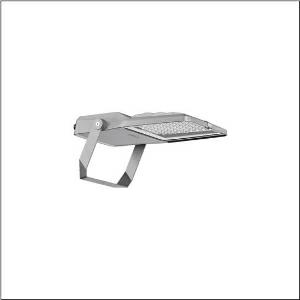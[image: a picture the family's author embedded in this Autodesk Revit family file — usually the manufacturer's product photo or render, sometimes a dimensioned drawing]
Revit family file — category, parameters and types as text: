
# Revit family: floodlight_fl_21_iq_mini___pl52_5xa7772d4d1a_6062
name_source: partatom
category: Lighting Fixtures
units: mm (PartAtom-declared; Revit-internal decimal feet)

## family parameters
Cut with Voids When Loaded = No
Host = Face
Light Source = No
Part Type = Normal
Room Calculation Point = No
Round Connector Dimension = Use Diameter
Shared = No

## types (1)
- --- (1 x LED, 18610 lm, 143 W, 4000K)
    Apparent Load = 143 VA
    CIE Flux Codes = 26 60 98 100 100
    Color Rendering = 70
    Color Temperature = 4000K
    Default Elevation = 1800 mm
    Description = Floodlight FL 21 iQ mini, floodlight, primary light control with lens, of PMMA, primary optical cover: protective disc, of toughened safety glass, transparent, light distribution: PL52, light emission: direct distribution, installation type: surface-mounted, LED, High Power LED, rated luminous flux: 18.610lm, luminous efficacy: 130lm/W, light colour: 740, colour temperature: 4000K, control gear: iQ Street-Remote/DALI, control: Street-Remote, Auto-Match, Temp-Guard, Night-Set, Smart-Wire, Desk-Remote (wireless, voltage-free reading and setting of iQ features in the workshop via application-optimized NFC function/RFID function), optimised constant luminous flux control (CLO 2.0), with terminal, 6-pole, mains connection: 220..240V, AC, 50/60Hz, start of lifetime: 143W, end of service life: 152W, reduction: 61W, luminaire housing, of diecast aluminium, powder-coated, Siteco® metallic grey (DB 702S), corrosivity category C5 mid according to DIN EN ISO 12944, suitable for swimming pools, chlorine-resistant, sealing non-destructively replaceable, mounting bracket, of steel, galvanised, powder-coated, Siteco® metallic grey (DB 702S), protection rating (complete): IP66, insulation class (complete): insulation class II (safety insulation), certification: CE, ENEC, VDE, protection symbol: D, impact resistance: IK08, permissible operating ambient temperature: -40..+40°C, permissible operating ambient temperature for outdoor applications: -40..+50°C, standard: DIN EN 12944, LABS conformity tested according to VDMA 24364:2018-05, packaging unit: 1 piece

Light Distribution: PL52
    Height = 70 mm
    Lamp = 1 x LED
    Lamp Light Flux = 18610 lm
    Lamp Power = 143 W
    Lamp count = 1
    Length = 485 mm
    Luminous efficacy = 130 lm/W
    Manufacturer = Siteco
    ModVariant = No
    Model = 5XA7772D4D1A
    Number of Poles = 1
    OnlyDefault = Yes
    Power Factor = 1
    Product Name = Floodlight FL 21 iQ mini | PL52
    Product group = floodlight | pylon annexe
    ProductGroupID = 6200
    Protection Class = Protection class II
    Protection Degree = IP 66
    RLX_Detail_Level = 1
    RLX_Emergency_Light_Flux = 0 lm
    RLX_Emergency_Type = 0
    RLX_Emergency_Type_DB = No
    RlxData = <blob elided: 96793 chars, md5=ac325bef>
    Socket = socket
    Standby Power = 0 W
    System Light Flux = 18610 lm
    System Power = 143 W
    Type Comments = factory setting: luminous flux: 100 % | dim-lin: 254 | 730 mA
    Type Image = l_1006845.jpg
    URL = http://relux.com
    VarID = @adj_163636
    Voltage = 0 V
    Weight = 0.00 kg
    Width = 337 mm

## geometry (parser evidence)
native form markers: Blend x4, Sweep x12
no freeform markers — native parametric forms only
